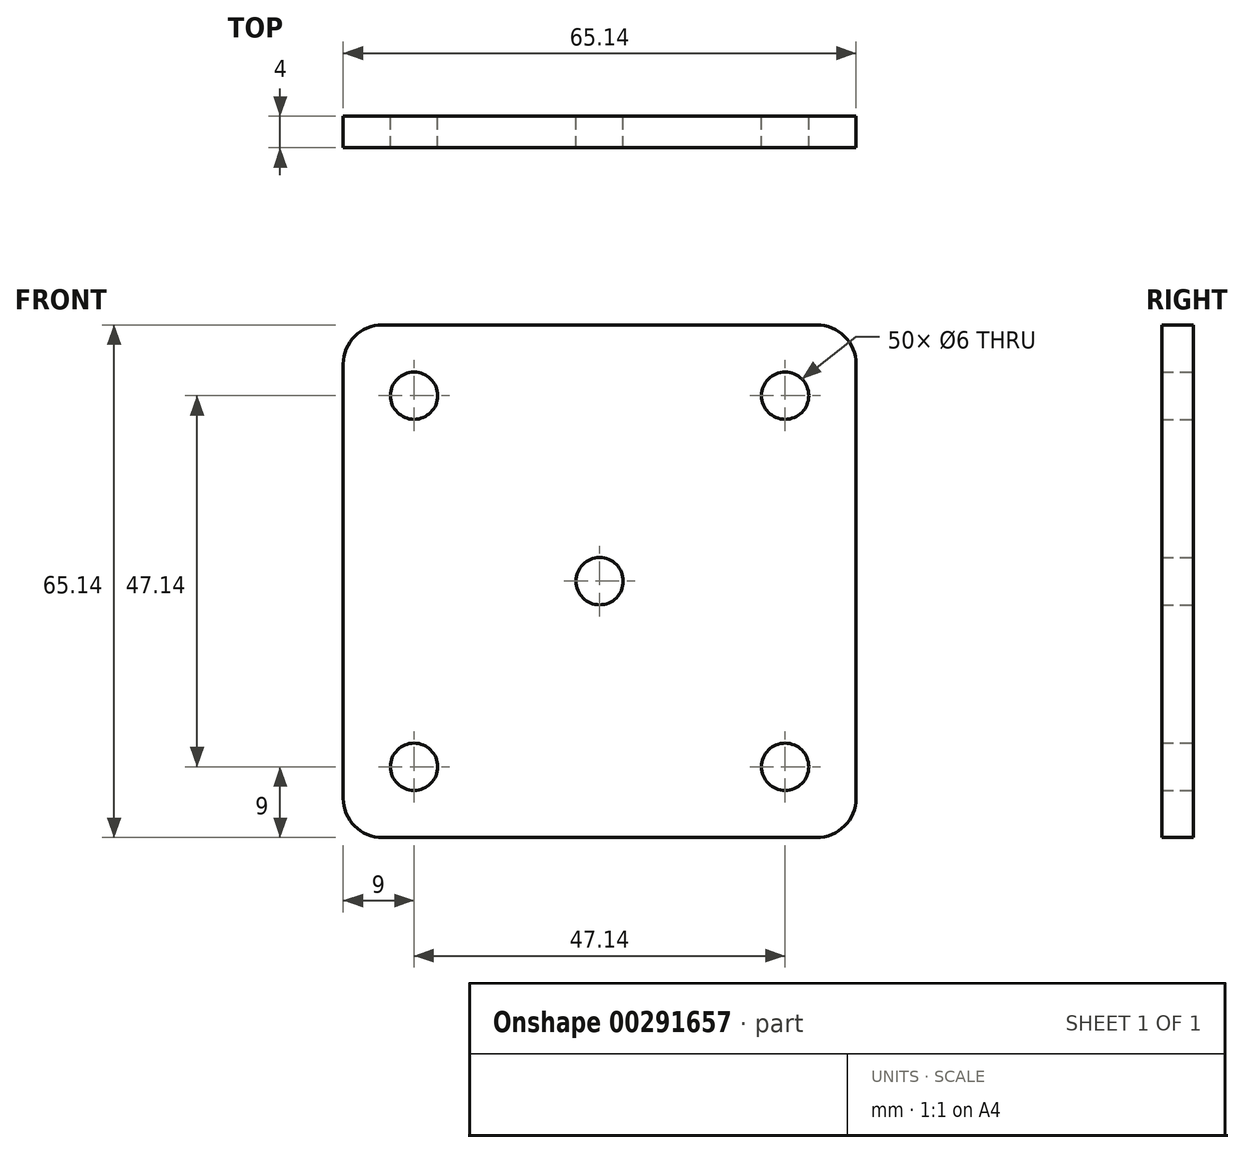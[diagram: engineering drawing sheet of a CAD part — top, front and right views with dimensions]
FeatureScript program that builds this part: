
annotation { "Feature Type Name" : "Feature", "Feature Type Description" : "" }
export const myFeature = defineFeature(function(context is Context, id is Id, definition is map)
    precondition{}
    {
        {
            var Q0;
            Q0=qCreatedBy(makeId("Front.planeOp"),FACE);
            var sketch = newSketch(context, id + "F0", { "sketchPlane" : qUnion([Q0])});
            skLineSegment(sketch, "E0.bottom", {"start": v(32.57, -32.57) * mm, "end": v(-32.57, -32.57) * mm});
            skLineSegment(sketch, "E0.top", {"start": v(32.57, 32.57) * mm, "end": v(-32.57, 32.57) * mm});
            skLineSegment(sketch, "E0.left", {"start": v(32.57, -32.57) * mm, "end": v(32.57, 32.57) * mm});
            skLineSegment(sketch, "E0.right", {"start": v(-32.57, -32.57) * mm, "end": v(-32.57, 32.57) * mm});
            skPoint(sketch, "E0.middle", {"position": v(0, 0) * mm});
            skCircle(sketch, "E1", {"center": v(0, 0) * mm, "radius": 3 * mm});
            skCircle(sketch, "E2", {"center": v(-23.57, 23.57) * mm, "radius": 3 * mm});
            skCircle(sketch, "E3", {"center": v(23.57, 23.57) * mm, "radius": 3 * mm});
            skCircle(sketch, "E4", {"center": v(-23.57, -23.57) * mm, "radius": 3 * mm});
            skCircle(sketch, "E5", {"center": v(23.57, -23.57) * mm, "radius": 3 * mm});
            skSolve(sketch);
        }
        {
            var Q0;
            Q0=makeQuery(id+"F0.imprint","IMPRINT",FACE,{"disambiguationData":[TD([[makeQuery(id+"F0.imprint","IMPRINT",EDGE,{"derivedFrom":sQuery(id+"F0.wireOp",EDGE,"E0.bottom")}),-1.0]])]});
            extrude(context, id + "F1", {"entities" : qUnion([Q0]), "depth" : 4 * mm});
        }
        {
            var Q0;
            Q0=makeQuery(id+"F1.opExtrude","SWEPT_EDGE",EDGE,{"disambiguationData":[OSD([sQuery(id+"F0.wireOp",EDGE,"E0.bottom"),sQuery(id+"F0.wireOp",EDGE,"E0.left")])]});
            var Q1;
            Q1=makeQuery(id+"F1.opExtrude","SWEPT_EDGE",EDGE,{"disambiguationData":[OSD([sQuery(id+"F0.wireOp",EDGE,"E0.bottom"),sQuery(id+"F0.wireOp",EDGE,"E0.right")])]});
            var Q2;
            Q2=makeQuery(id+"F1.opExtrude","SWEPT_EDGE",EDGE,{"disambiguationData":[OSD([sQuery(id+"F0.wireOp",EDGE,"E0.top"),sQuery(id+"F0.wireOp",EDGE,"E0.right")])]});
            var Q3;
            Q3=makeQuery(id+"F1.opExtrude","SWEPT_EDGE",EDGE,{"disambiguationData":[OSD([sQuery(id+"F0.wireOp",EDGE,"E0.top"),sQuery(id+"F0.wireOp",EDGE,"E0.left")])]});
            fillet(context, id + "F2", {"entities" : qUnion([Q0, Q1, Q2, Q3]), "radius" : 5 * mm, "tangentPropagation" : true, "allowEdgeOverflow" : false});
        }
    });
